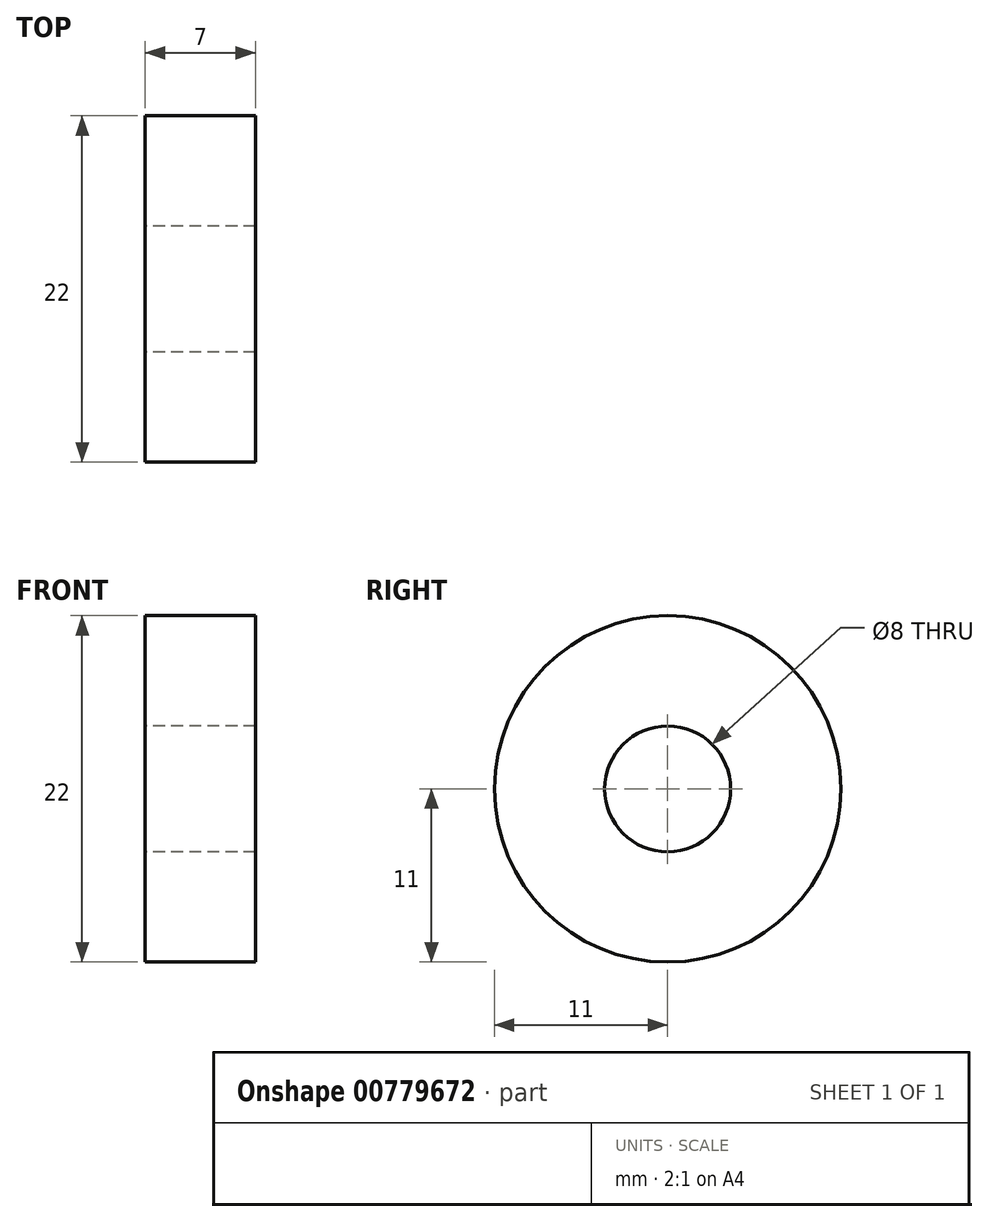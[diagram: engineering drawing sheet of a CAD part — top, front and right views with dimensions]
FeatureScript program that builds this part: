
annotation { "Feature Type Name" : "Feature", "Feature Type Description" : "" }
export const myFeature = defineFeature(function(context is Context, id is Id, definition is map)
    precondition{}
    {
        {
            var Q0;
            Q0=qCreatedBy(makeId("Right.planeOp"),FACE);
            var sketch = newSketch(context, id + "F0", { "sketchPlane" : qUnion([Q0])});
            skCircle(sketch, "E0", {"center": v(0, 0) * mm, "radius": 11 * mm});
            skCircle(sketch, "E1", {"center": v(0, 0) * mm, "radius": 4 * mm});
            skSolve(sketch);
        }
        {
            var Q0;
            Q0 = qSketchRegion(id + "F0", true);
            extrude(context, id + "F1", {"entities" : qUnion([Q0]), "endBound" : BoundingType.SYMMETRIC, "depth" : 7 * mm, "offsetDistance" : 25 * mm});
        }
    });
